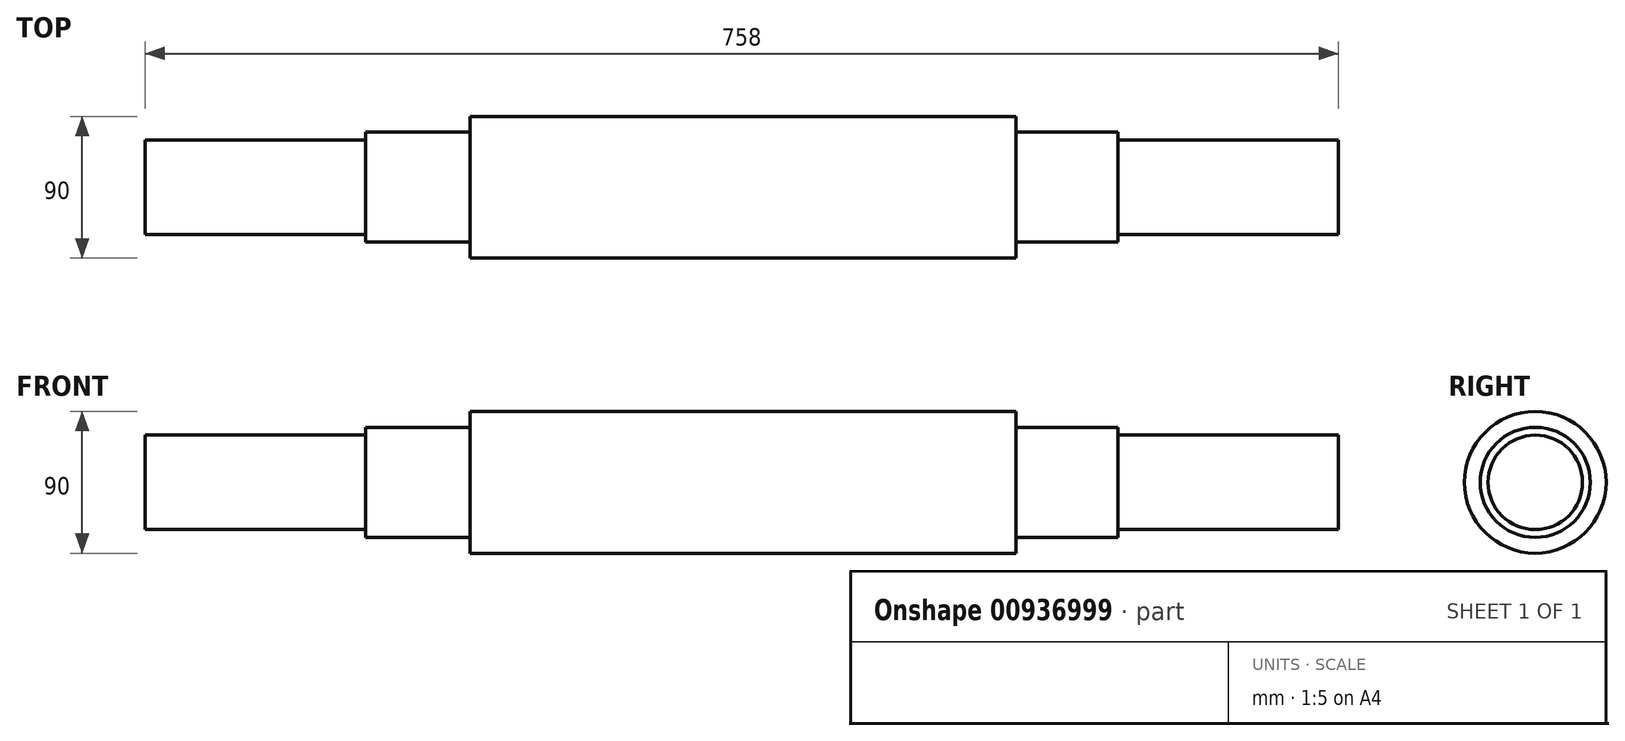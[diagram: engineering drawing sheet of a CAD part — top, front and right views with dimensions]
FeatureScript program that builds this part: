
annotation { "Feature Type Name" : "Feature", "Feature Type Description" : "" }
export const myFeature = defineFeature(function(context is Context, id is Id, definition is map)
    precondition{}
    {
        {
            var Q0;
            Q0=qCreatedBy(makeId("Front.planeOp"),FACE);
            var sketch = newSketch(context, id + "F0", { "sketchPlane" : qUnion([Q0])});
            skLineSegment(sketch, "E0.bottom", {"start": v(-132.63, 0) * mm, "end": v(213.87, 0) * mm});
            skLineSegment(sketch, "E0.top", {"start": v(-132.63, 45) * mm, "end": v(213.87, 45) * mm});
            skLineSegment(sketch, "E0.left", {"start": v(-132.63, 0) * mm, "end": v(-132.63, 45) * mm});
            skLineSegment(sketch, "E0.right", {"start": v(213.87, 0) * mm, "end": v(213.87, 45) * mm});
            skLineSegment(sketch, "E1.bottom", {"start": v(-132.63, 35) * mm, "end": v(-199.13, 35) * mm});
            skLineSegment(sketch, "E1.top", {"start": v(-132.63, 0) * mm, "end": v(-199.13, 0) * mm});
            skLineSegment(sketch, "E1.left", {"start": v(-132.63, 35) * mm, "end": v(-132.63, 0) * mm});
            skLineSegment(sketch, "E1.right", {"start": v(-199.13, 35) * mm, "end": v(-199.13, 0) * mm});
            skLineSegment(sketch, "E2.bottom", {"start": v(213.87, 0) * mm, "end": v(278.87, 0) * mm});
            skLineSegment(sketch, "E2.top", {"start": v(213.87, 35) * mm, "end": v(278.87, 35) * mm});
            skLineSegment(sketch, "E2.left", {"start": v(213.87, 0) * mm, "end": v(213.87, 35) * mm});
            skLineSegment(sketch, "E2.right", {"start": v(278.87, 0) * mm, "end": v(278.87, 35) * mm});
            skSolve(sketch);
        }
        {
            var Q0;
            Q0=makeQuery(id+"F0.imprint","IMPRINT",FACE,{"disambiguationData":[TD([[makeQuery(id+"F0.imprint","IMPRINT",EDGE,{"derivedFrom":sQuery(id+"F0.wireOp",EDGE,"E1.bottom")}),1.0]])]});
            var Q1;
            Q1=makeQuery(id+"F0.imprint","IMPRINT",FACE,{"disambiguationData":[TD([[makeQuery(id+"F0.imprint","IMPRINT",EDGE,{"derivedFrom":sQuery(id+"F0.wireOp",EDGE,"E0.bottom")}),1.0]])]});
            var Q2;
            Q2=makeQuery(id+"F0.imprint","IMPRINT",FACE,{"disambiguationData":[TD([[makeQuery(id+"F0.imprint","IMPRINT",EDGE,{"derivedFrom":sQuery(id+"F0.wireOp",EDGE,"E2.bottom")}),1.0]])]});
            var Q3;
            Q3=sQuery(id+"F0.wireOp",EDGE,"E0.bottom");
            revolve(context, id + "F1", {"surfaceOperationType" : NewSurfaceOperationType.NEW, "entities" : qUnion([Q0, Q1, Q2]), "axis" : qUnion([Q3]), "revolveType" : RevolveType.FULL});
        }
        {
            var Q0;
            Q0=makeQuery(id+"F1.opRevolve","SWEPT_FACE",FACE,{"disambiguationData":[OSD([sQuery(id+"F0.wireOp",EDGE,"E1.right")])]});
            var sketch = newSketch(context, id + "F2", { "sketchPlane" : qUnion([Q0])});
            skCircle(sketch, "E3", {"center": v(0, 0) * mm, "radius": 30 * mm});
            skSolve(sketch);
        }
        {
            var Q0;
            Q0 = qSketchRegion(id + "F2", true);
            extrude(context, id + "F3", {"entities" : qUnion([Q0]), "operationType" : NewBodyOperationType.ADD, "depth" : 140 * mm, "offsetDistance" : 25 * mm});
        }
        {
            var Q0;
            Q0=makeQuery(id+"F1.opRevolve","SWEPT_FACE",FACE,{"disambiguationData":[OSD([sQuery(id+"F0.wireOp",EDGE,"E2.right")])]});
            var sketch = newSketch(context, id + "F4", { "sketchPlane" : qUnion([Q0])});
            skCircle(sketch, "E4", {"center": v(0, 0) * mm, "radius": 30 * mm});
            skSolve(sketch);
        }
        {
            var Q0;
            Q0=makeQuery(id+"F4.imprint","IMPRINT",FACE,{"disambiguationData":[TD([[makeQuery(id+"F4.imprint","IMPRINT",EDGE,{"derivedFrom":sQuery(id+"F4.wireOp",EDGE,"E4")}),1.0]])]});
            extrude(context, id + "F5", {"entities" : qUnion([Q0]), "operationType" : NewBodyOperationType.ADD, "depth" : 140 * mm, "offsetDistance" : 25 * mm});
        }
    });
